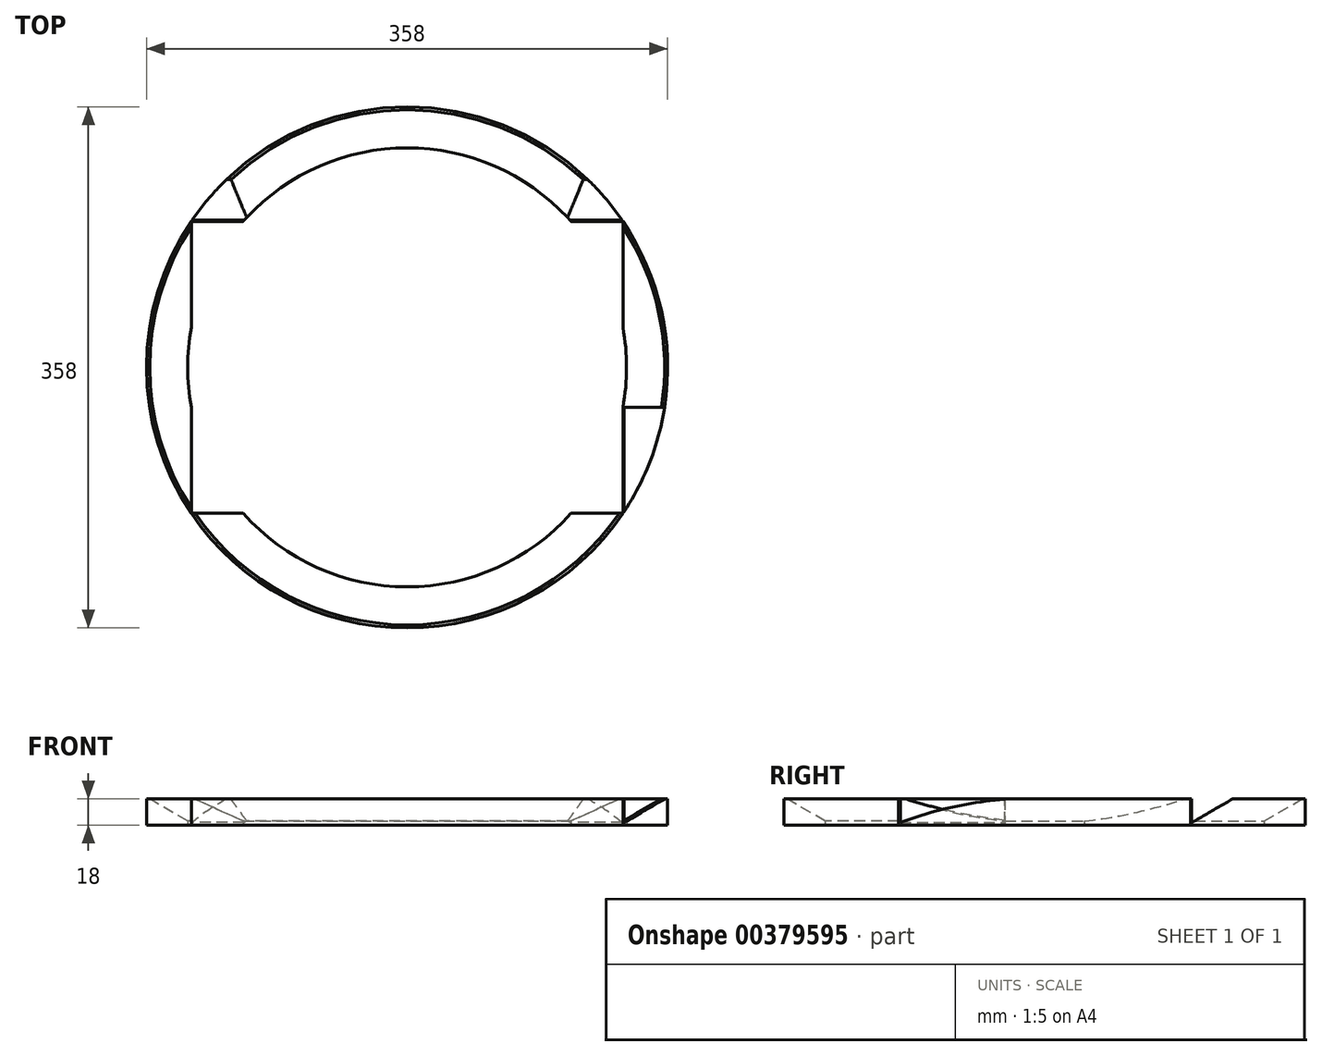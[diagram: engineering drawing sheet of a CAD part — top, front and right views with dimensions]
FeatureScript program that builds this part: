
annotation { "Feature Type Name" : "Feature", "Feature Type Description" : "" }
export const myFeature = defineFeature(function(context is Context, id is Id, definition is map)
    precondition{}
    {
        {
            assignVariable(context, id + "F0", {"name" : "L300Real", "anyValue" : 314});
        }
        {
            assignVariable(context, id + "F1", {"name" : "ContOffset", "anyValue" : 8});
        }
        {
            var Q0;
            Q0=qCreatedBy(makeId("Top.planeOp"),FACE);
            var sketch = newSketch(context, id + "F2", { "sketchPlane" : qUnion([Q0])});
            skLineSegment(sketch, "E0.bottom", {"start": v(-157, 109) * mm, "end": v(-116.44, 109) * mm});
            skLineSegment(sketch, "E0.top", {"start": v(-157, -109) * mm, "end": v(-116.44, -109) * mm});
            skLineSegment(sketch, "E0.left", {"start": v(-157, 109) * mm, "end": v(-157, 28.13) * mm});
            skLineSegment(sketch, "E0.right", {"start": v(157, 109) * mm, "end": v(157, 28.13) * mm});
            skPoint(sketch, "E0.middle", {"position": v(0, 0) * mm});
            skArc(sketch, "E1", {"start": v(-157, 28.13) * mm, "mid": v(-159.5, 0) * mm, "end": v(-157, -28.13) * mm});
            skLineSegment(sketch, "E2.trimOffspring", {"start": v(116.44, 109) * mm, "end": v(157, 109) * mm});
            skArc(sketch, "E3.trimOffspring", {"start": v(116.44, 109) * mm, "mid": v(0, 159.5) * mm, "end": v(-116.44, 109) * mm});
            skLineSegment(sketch, "E4.trimOffspring", {"start": v(157, -28.13) * mm, "end": v(157, -109) * mm});
            skArc(sketch, "E5.trimOffspring", {"start": v(157, -28.13) * mm, "mid": v(159.5, 0) * mm, "end": v(157, 28.13) * mm});
            skLineSegment(sketch, "E6.trimOffspring", {"start": v(116.44, -109) * mm, "end": v(157, -109) * mm});
            skArc(sketch, "E7.trimOffspring", {"start": v(-116.44, -109) * mm, "mid": v(0, -159.5) * mm, "end": v(116.44, -109) * mm});
            skLineSegment(sketch, "E8.trimOffspring", {"start": v(-157, -28.13) * mm, "end": v(-157, -109) * mm});
            skLineSegment(sketch, "E9.0", {"start": v(112.6, 100.28) * mm, "end": v(148.28, 100.28) * mm});
            skLineSegment(sketch, "E9.1", {"start": v(-148.28, -27.34) * mm, "end": v(-148.28, -100.28) * mm});
            skArc(sketch, "E9.2", {"start": v(-148.28, 27.34) * mm, "mid": v(-150.78, 0) * mm, "end": v(-148.28, -27.34) * mm});
            skLineSegment(sketch, "E9.3", {"start": v(-148.28, 100.28) * mm, "end": v(-148.28, 27.34) * mm});
            skLineSegment(sketch, "E9.4", {"start": v(-148.28, 100.28) * mm, "end": v(-112.6, 100.28) * mm});
            skLineSegment(sketch, "E9.5", {"start": v(-148.28, -100.28) * mm, "end": v(-112.6, -100.28) * mm});
            skArc(sketch, "E9.6", {"start": v(112.6, 100.28) * mm, "mid": v(0, 150.78) * mm, "end": v(-112.6, 100.28) * mm});
            skArc(sketch, "E9.7", {"start": v(-112.6, -100.28) * mm, "mid": v(0, -150.78) * mm, "end": v(112.6, -100.28) * mm});
            skLineSegment(sketch, "E9.8", {"start": v(112.6, -100.28) * mm, "end": v(148.28, -100.28) * mm});
            skLineSegment(sketch, "E9.9", {"start": v(148.28, -27.34) * mm, "end": v(148.28, -100.28) * mm});
            skArc(sketch, "E9.10", {"start": v(148.28, -27.34) * mm, "mid": v(150.78, 0) * mm, "end": v(148.28, 27.34) * mm});
            skLineSegment(sketch, "E9.11", {"start": v(148.28, 100.28) * mm, "end": v(148.28, 27.34) * mm});
            skCircle(sketch, "E10", {"center": v(0, 0) * mm, "radius": 179 * mm});
            skSolve(sketch);
        }
        {
            var Q0;
            {var subQ4=sQuery(id+"F2.wireOp",EDGE,"E3.trimOffspring");Q0=makeQuery(id+"F2.imprint","IMPRINT",FACE,{"disambiguationData":[TD([[makeQuery(id+"F2.imprint","IMPRINT",EDGE,{"derivedFrom":subQ4}),1.0]])]});}
            var Q1;
            {var subQ0=sQuery(id+"F2.wireOp",EDGE,"E3.trimOffspring");Q1=makeQuery(id+"F2.imprint","IMPRINT",FACE,{"disambiguationData":[TD([[makeQuery(id+"F2.imprint","IMPRINT",EDGE,{"derivedFrom":subQ0}),-1.0]])]});}
            var Q2;
            {var subQ5=sQuery(id+"F2.wireOp",EDGE,"E1");Q2=makeQuery(id+"F2.imprint","IMPRINT",FACE,{"disambiguationData":[TD([[makeQuery(id+"F2.imprint","IMPRINT",EDGE,{"derivedFrom":subQ5}),1.0]])]});}
            var Q3;
            {var subQ0=sQuery(id+"F2.wireOp",EDGE,"E1");Q3=makeQuery(id+"F2.imprint","IMPRINT",FACE,{"disambiguationData":[TD([[makeQuery(id+"F2.imprint","IMPRINT",EDGE,{"derivedFrom":subQ0}),-1.0]])]});}
            var Q4;
            {var subQ0=sQuery(id+"F2.wireOp",EDGE,"E7.trimOffspring");Q4=makeQuery(id+"F2.imprint","IMPRINT",FACE,{"disambiguationData":[TD([[makeQuery(id+"F2.imprint","IMPRINT",EDGE,{"derivedFrom":subQ0}),-1.0]])]});}
            var Q5;
            {var subQ0=sQuery(id+"F2.wireOp",EDGE,"E7.trimOffspring");Q5=makeQuery(id+"F2.imprint","IMPRINT",FACE,{"disambiguationData":[TD([[makeQuery(id+"F2.imprint","IMPRINT",EDGE,{"derivedFrom":subQ0}),1.0]])]});}
            var Q6;
            {var subQ4=sQuery(id+"F2.wireOp",EDGE,"E5.trimOffspring");Q6=makeQuery(id+"F2.imprint","IMPRINT",FACE,{"disambiguationData":[TD([[makeQuery(id+"F2.imprint","IMPRINT",EDGE,{"derivedFrom":subQ4}),1.0]])]});}
            var Q7;
            {var subQ0=sQuery(id+"F2.wireOp",EDGE,"E5.trimOffspring");Q7=makeQuery(id+"F2.imprint","IMPRINT",FACE,{"disambiguationData":[TD([[makeQuery(id+"F2.imprint","IMPRINT",EDGE,{"derivedFrom":subQ0}),-1.0]])]});}
            extrude(context, id + "F3", {"entities" : qUnion([Q0, Q1, Q2, Q3, Q4, Q5, Q6, Q7]), "depth" : 18 * mm});
        }
        {
            var Q0;
            Q0=qCreatedBy(makeId("Front.planeOp"),FACE);
            var sketch = newSketch(context, id + "F4", { "sketchPlane" : qUnion([Q0])});
            skLineSegment(sketch, "E11", {"start": v(0, 1.8) * mm, "end": v(-148.82, 1.8) * mm});
            skLineSegment(sketch, "E12", {"start": v(-148.82, 1.8) * mm, "end": v(-180, 19.8) * mm});
            skLineSegment(sketch, "E13", {"start": v(-180, 19.8) * mm, "end": v(0, 19.8) * mm});
            skLineSegment(sketch, "E14", {"start": v(0, 19.8) * mm, "end": v(0, 1.8) * mm});
            skSolve(sketch);
        }
        {
            var Q0;
            Q0 = qSketchRegion(id + "F4", true);
            var Q1;
            Q1=sQuery(id+"F4.wireOp",EDGE,"E14");
            revolve(context, id + "F5", {"operationType" : NewBodyOperationType.REMOVE, "entities" : qUnion([Q0]), "axis" : qUnion([Q1]), "revolveType" : RevolveType.FULL, "oppositeDirection" : true});
        }
        {
            var Q0;
            Q0=qCreatedBy(makeId("Right.planeOp"),FACE);
            var sketch = newSketch(context, id + "F6", { "sketchPlane" : qUnion([Q0])});
            skLineSegment(sketch, "E15", {"start": v(101, 1.8) * mm, "end": v(132.18, 19.8) * mm});
            skLineSegment(sketch, "E16", {"start": v(132.18, 19.8) * mm, "end": v(101, 19.8) * mm});
            skLineSegment(sketch, "E17", {"start": v(101, 19.8) * mm, "end": v(101, 1.8) * mm});
            skSolve(sketch);
        }
        {
            var Q0;
            Q0 = qSketchRegion(id + "F6", true);
            extrude(context, id + "F7", {"entities" : qUnion([Q0]), "operationType" : NewBodyOperationType.REMOVE, "endBound" : BoundingType.SYMMETRIC, "depth" : (getVariable(context, 'L300Real') - getVariable(context, 'ContOffset')) * mm});
        }
        {
            var Q0;
            Q0=qCreatedBy(makeId("Front.planeOp"),FACE);
            cPlane(context, id + "F8", {"entities" : qUnion([Q0]), "cplaneType" : CPlaneType.OFFSET, "offset" : 27.47 * mm, "width" : 150 * mm, "height" : 150 * mm});
        }
        {
            var Q0;
            Q0=qCreatedBy(id+"F8.planeOp",FACE);
            var sketch = newSketch(context, id + "F9", { "sketchPlane" : qUnion([Q0])});
            skLineSegment(sketch, "E18", {"start": v(149, 1.8) * mm, "end": v(180.18, 19.8) * mm});
            skLineSegment(sketch, "E19", {"start": v(180.18, 19.8) * mm, "end": v(149, 19.8) * mm});
            skLineSegment(sketch, "E20", {"start": v(149, 19.8) * mm, "end": v(149, 1.8) * mm});
            skSolve(sketch);
        }
        {
            var Q0;
            Q0 = qSketchRegion(id + "F9", true);
            extrude(context, id + "F10", {"entities" : qUnion([Q0]), "operationType" : NewBodyOperationType.REMOVE, "depth" : 76 * mm});
        }
    });
